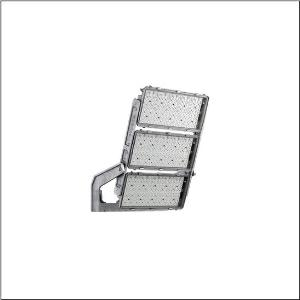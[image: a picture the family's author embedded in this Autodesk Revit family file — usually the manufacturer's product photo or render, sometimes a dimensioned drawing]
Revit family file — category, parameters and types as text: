
# Revit family: floodlight_fl_11_maxi_pro_remote___pl43_5xa779524a01aa_32ee
name_source: partatom
category: Lighting Fixtures
units: mm (PartAtom-declared; Revit-internal decimal feet)

## family parameters
Cut with Voids When Loaded = No
Host = Face
Light Source = No
Part Type = Normal
Room Calculation Point = No
Round Connector Dimension = Use Diameter
Shared = No

## types (1)
- --- (1 x LED, 130000 lm, 1334.7 W, 5700K)
    Apparent Load = 1335 VA
    CIE Flux Codes = 25 74 99 100 100
    Color Rendering = 90
    Color Temperature = 5700K
    Default Elevation = 1800 mm
    Description = Floodlight FL 11  maxi  pro Remote floodlight; light control with lens of PMMA; cover panel of toughened safety glass, transparent; light distribution: PL43, asymmetric direct distribution, LEDcolour temperature: 5700K, rated luminous flux: 130.000lm, colour rendering: CRI > 90, light colour: 957; luminous efficacy: 97lm/W; brightness control: DMX+RDM; with terminal, 8-pole, max. 2.5mm², mains connection: 220..240V/380..400V AC, 50/60Hz, surge voltage resistance: line to ground: 10kV, ECG replaceable separately, no afterglow with DALI off / DMX off command, LED unit replaceable without ESD environment, dustproof LED module, dimming range 10..100%; 1335W floodlight with 3x LED unit of diecast aluminium, coated grey; length: 713mm / width: 651mm / height: 338mm; mounting bracket, of diecast aluminium, uncoated, natural, equipment: Power, protection rating (complete): IP66; insulation class (complete): insulation class I (protective earthing); certification: CE, ENEC, VDE; ball protection: ball impact resistance with accessories, impact resistance: IK07; only for outdoor installations, rated ambient temperature 10°C, permissible operating ambient temperature: -40..+30°C, permissible storage temperature: -40..+85°C; packaging unit: 1 piece

Light Distribution: PL43
    Height = 320 mm
    Lamp = 1 x LED
    Lamp Light Flux = 130000 lm
    Lamp Power = 1334.7 W
    Lamp count = 1
    Length = 1002 mm
    Luminous efficacy = 97 lm/W
    Manufacturer = Siteco
    ModVariant = No
    Model = 5XA779524A01AA
    Mounting Place = Ceiling
    Mounting Type = Surface mounted
    Number of Poles = 1
    OnlyDefault = Yes
    Power Factor = 1
    Product Name = Floodlight FL 11 maxi pro Remote | PL43
    Product group = floodlight | ceiling mounted
    ProductGroupID = 302
    Protection Class = Protection class I
    Protection Degree = IP 66
    RLX_Detail_Level = 1
    RLX_Emergency_Light_Flux = 0 lm
    RLX_Emergency_Type = 0
    RLX_Emergency_Type_DB = No
    RlxData = <blob elided: 52501 chars, md5=22a9d6bf>
    Socket = socket
    Standby Power = 0 W
    System Light Flux = 130000 lm
    System Power = 1335 W
    Type Comments = factory setting: luminous flux: 100 % | dim-lin: 255 | 920 mA
    Type Image = l_1006784.jpg
    URL = http://relux.com
    VarID = @adj_065443
    Voltage = 0 V
    Weight = 0.00 kg
    Width = 655 mm

## geometry (parser evidence)
native form markers: Blend x4, Sweep x13
no freeform markers — native parametric forms only
